# Revit family: Planting_Area_Drain-Jay R. Smith-Round_Type-1909_Series
name_source: partatom
category: Plumbing Fixtures
units: mm (PartAtom-declared; Revit-internal decimal feet)

## family parameters
Always vertical = Yes
Cut with Voids When Loaded = No
OmniClass Number = 23.70.50.21.24
OmniClass Title = Waste Water Drains
Part Type = Normal
Room Calculation Point = No
Round Connector Dimension = Use Diameter
Shared = No
Work Plane-Based = Yes

## types (9) — shared parameters
AD - Aluminum Dome = No
Assembly Code = D2030300
CID - Cast Iron Dome = No
CIDG - Galvanized Cast Iron Dome = No
CW Connection = No
Default Elevation = 0"
Description = Planter Area Drain for Multi-Levels
Diameter = 15 1/4"
Dome Height = 4 1/4"
Dome Material = ABS-Jay R Smith-Black
Finish = Cast Iron-Jay R Smith-Duco Coated
G - Galvanized Cast Iron Body & Collar = No
HW Connection = No
Installation Type = Roof/Floor Mounted
L - Speedi-Set Service Weight = No
LXH - Speedi-Set Extra Heavy = No
Manufacturer = Jay R. Smith Mfg. Co.
Material = Cast Iron-Jay R Smith-Duco Coated
Perforated Pipe Diameter = 4"
Product Documentation Link = https://www.jrsmith.com
Product Page URL = https://www.jrsmith.com
RBD - Rough Bronze Dome = No
SP - Solid Standpipe = No
SSM - Standpipe Covered with Stainless Steel Mesh = No
Standpipe Material = Plastic-Jay R Smith-Perforated
URL = http://www.jrsmith.com
Vent Connection = No
WSH-with Seepage Holes in Flashing = No
Waste Connection = Yes

## per-type parameters (varying)
| type | B Dimension | Connection Outlet Description | Connection Radius | Connection Size |
| 1909Y02 | 5" | 2" No-HUB Outlet Connection | 1" | 2" |
| 1909Y03 | 5" | 3" No-HUB Outlet Connection | 1 1/2" | 3" |
| 1909Y04 | 5" | 4" No-HUB Outlet Connection | 2" | 4" |
| 1909C02 | 5" | 2" Caulk Outlet Connection | 1" | 2" |
| 1909C03 | 5" | 3" Caulk Outlet Connection | 1 1/2" | 3" |
| 1909C04 | 5" | 4" Caulk Outlet Connection | 2" | 4" |
| 1909T02 | 3 3/4" | 2" Threaded Outlet Connection | 1" | 2" |
| 1909T03 | 3 3/4" | 3" Threaded Outlet Connection | 1 1/2" | 3" |
| 1909T04 | 3 3/4" | 4" Threaded Outlet Connection | 2" | 4" |

note: column(s) folded — value = type name in every type: Model

## geometry (parser evidence)
native form markers: Sweep x2
no freeform markers — native parametric forms only
